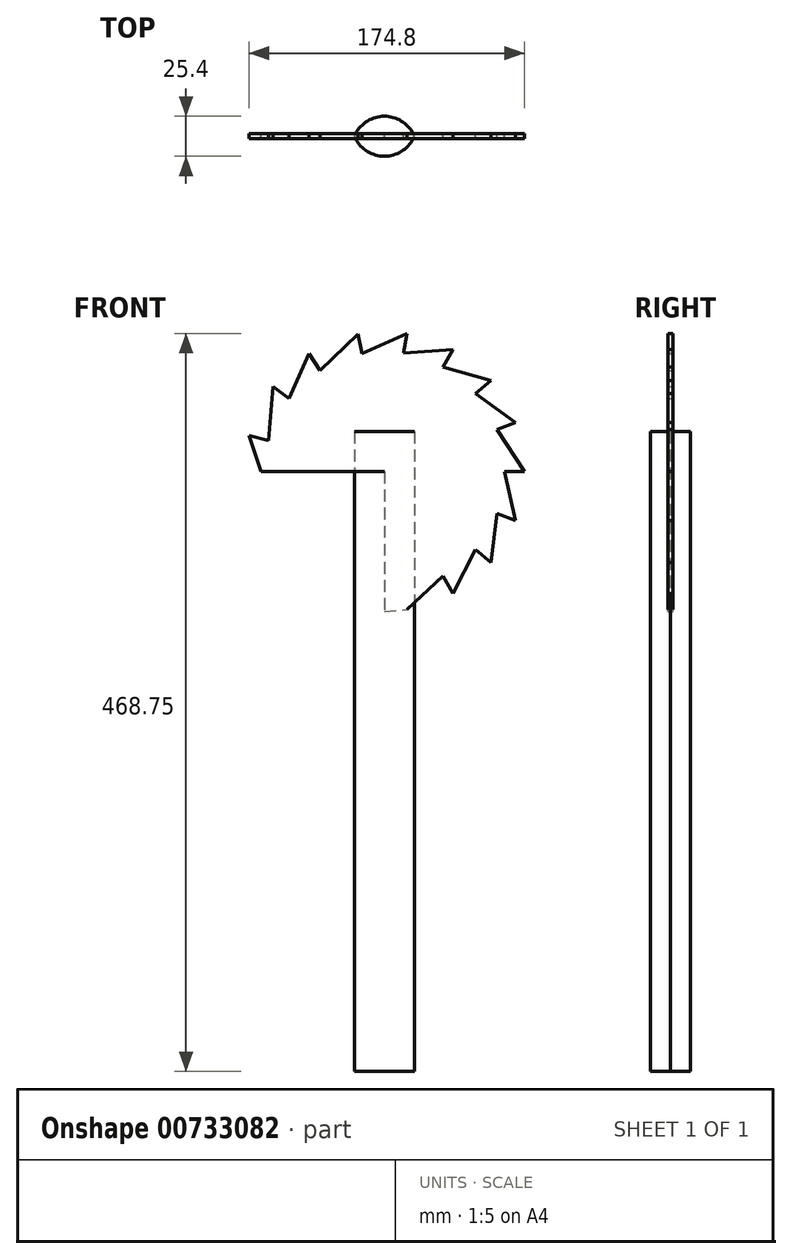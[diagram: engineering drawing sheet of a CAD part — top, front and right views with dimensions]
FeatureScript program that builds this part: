
annotation { "Feature Type Name" : "Feature", "Feature Type Description" : "" }
export const myFeature = defineFeature(function(context is Context, id is Id, definition is map)
    precondition{}
    {
        {
            var Q0;
            Q0=qCreatedBy(makeId("Top.planeOp"),FACE);
            var sketch = newSketch(context, id + "F0", { "sketchPlane" : qUnion([Q0])});
            skArc(sketch, "E0", {"start": v(19.05, 0) * mm, "mid": v(0, 12.7) * mm, "end": v(-19.05, 0) * mm});
            skArc(sketch, "E1", {"start": v(-19.05, 0) * mm, "mid": v(0, -12.7) * mm, "end": v(19.05, 0) * mm});
            skSolve(sketch);
        }
        {
            var Q0;
            Q0=makeQuery(id+"F0.imprint","IMPRINT",FACE,{"disambiguationData":[TD([[makeQuery(id+"F0.imprint","IMPRINT",EDGE,{"derivedFrom":sQuery(id+"F0.wireOp",EDGE,"E0")}),1.0]])]});
            extrude(context, id + "F1", {"entities" : qUnion([Q0]), "depth" : 406.4 * mm, "offsetDistance" : 25.4 * mm});
        }
        {
            var Q0;
            Q0=qCreatedBy(makeId("Front.planeOp"),FACE);
            var sketch = newSketch(context, id + "F2", { "sketchPlane" : qUnion([Q0])});
            skArc(sketch, "E2", {"start": v(0, 292.1) * mm, "mid": v(59.92, 446.67) * mm, "end": v(-88.53, 372.88) * mm, "construction": true});
            skLineSegment(sketch, "E3", {"start": v(0, 381) * mm, "end": v(43.57, 303.51) * mm, "construction": true});
            skLineSegment(sketch, "E4", {"start": v(0, 381) * mm, "end": v(67.56, 323.21) * mm, "construction": true});
            skLineSegment(sketch, "E5", {"start": v(0, 381) * mm, "end": v(83.3, 349.96) * mm, "construction": true});
            skLineSegment(sketch, "E6", {"start": v(0, 381) * mm, "end": v(88.9, 381) * mm, "construction": true});
            skLineSegment(sketch, "E7", {"start": v(0, 381) * mm, "end": v(83.3, 412.04) * mm, "construction": true});
            skLineSegment(sketch, "E8", {"start": v(0, 381) * mm, "end": v(67.56, 438.79) * mm, "construction": true});
            skLineSegment(sketch, "E9", {"start": v(0, 381) * mm, "end": v(43.57, 458.49) * mm, "construction": true});
            skLineSegment(sketch, "E10", {"start": v(0, 381) * mm, "end": v(14.28, 468.75) * mm, "construction": true});
            skLineSegment(sketch, "E11", {"start": v(-16.76, 468.3) * mm, "end": v(0, 381) * mm, "construction": true});
            skLineSegment(sketch, "E12", {"start": v(-47.8, 455.96) * mm, "end": v(0, 381) * mm, "construction": true});
            skLineSegment(sketch, "E13", {"start": v(-70.65, 434.96) * mm, "end": v(0, 381) * mm, "construction": true});
            skLineSegment(sketch, "E14", {"start": v(-85.9, 403.92) * mm, "end": v(0, 381) * mm, "construction": true});
            skLineSegment(sketch, "E15", {"start": v(14.28, 293.25) * mm, "end": v(0, 381) * mm, "construction": true});
            skLineSegment(sketch, "E16", {"start": v(0, 381) * mm, "end": v(-88.9, 381) * mm});
            skLineSegment(sketch, "E17", {"start": v(0, 381) * mm, "end": v(0, 292.1) * mm});
            skPoint(sketch, "E18.start.orphan", {"position": v(-79.81, 341.84) * mm});
            skPoint(sketch, "E19.start.orphan", {"position": v(-54.55, 310.8) * mm});
            skPoint(sketch, "E20.start.orphan", {"position": v(-27.09, 296.33) * mm});
            skLineSegment(sketch, "E21", {"start": v(14.28, 293.25) * mm, "end": v(37.35, 314.58) * mm});
            skLineSegment(sketch, "E22", {"start": v(37.35, 314.58) * mm, "end": v(43.57, 303.51) * mm});
            skLineSegment(sketch, "E23", {"start": v(57.9, 331.47) * mm, "end": v(43.57, 303.51) * mm});
            skLineSegment(sketch, "E24", {"start": v(67.56, 323.21) * mm, "end": v(57.9, 331.47) * mm});
            skLineSegment(sketch, "E25", {"start": v(83.3, 349.96) * mm, "end": v(71.4, 354.4) * mm});
            skLineSegment(sketch, "E26", {"start": v(71.4, 354.4) * mm, "end": v(67.56, 323.21) * mm});
            skLineSegment(sketch, "E27", {"start": v(88.9, 381) * mm, "end": v(76.2, 381) * mm});
            skLineSegment(sketch, "E28", {"start": v(76.2, 381) * mm, "end": v(83.3, 349.96) * mm});
            skLineSegment(sketch, "E29", {"start": v(83.3, 412.04) * mm, "end": v(71.4, 407.6) * mm});
            skLineSegment(sketch, "E30", {"start": v(71.4, 407.6) * mm, "end": v(88.9, 381) * mm});
            skLineSegment(sketch, "E31", {"start": v(67.56, 438.79) * mm, "end": v(57.9, 430.53) * mm});
            skLineSegment(sketch, "E32", {"start": v(57.9, 430.53) * mm, "end": v(83.3, 412.04) * mm});
            skLineSegment(sketch, "E33", {"start": v(43.57, 458.49) * mm, "end": v(37.35, 447.42) * mm});
            skLineSegment(sketch, "E34", {"start": v(37.35, 447.42) * mm, "end": v(67.56, 438.79) * mm});
            skLineSegment(sketch, "E35", {"start": v(14.28, 468.75) * mm, "end": v(12.24, 456.21) * mm});
            skLineSegment(sketch, "E36", {"start": v(12.24, 456.21) * mm, "end": v(43.57, 458.49) * mm});
            skLineSegment(sketch, "E37", {"start": v(-16.76, 468.3) * mm, "end": v(-14.37, 455.83) * mm});
            skLineSegment(sketch, "E38", {"start": v(-14.37, 455.83) * mm, "end": v(14.28, 468.75) * mm});
            skLineSegment(sketch, "E39", {"start": v(-47.8, 455.96) * mm, "end": v(-40.97, 445.25) * mm});
            skLineSegment(sketch, "E40", {"start": v(-40.97, 445.25) * mm, "end": v(-16.76, 468.3) * mm});
            skLineSegment(sketch, "E41", {"start": v(-70.65, 434.96) * mm, "end": v(-60.56, 427.25) * mm});
            skLineSegment(sketch, "E42", {"start": v(-60.56, 427.25) * mm, "end": v(-47.8, 455.96) * mm});
            skLineSegment(sketch, "E43", {"start": v(-85.9, 403.92) * mm, "end": v(-73.62, 400.64) * mm});
            skLineSegment(sketch, "E44", {"start": v(-73.62, 400.64) * mm, "end": v(-70.65, 434.96) * mm});
            skLineSegment(sketch, "E45", {"start": v(-75.9, 374.13) * mm, "end": v(-85.9, 403.92) * mm});
            skLineSegment(sketch, "E46", {"start": v(-88.53, 372.88) * mm, "end": v(-75.9, 374.13) * mm, "construction": true});
            skLineSegment(sketch, "E47", {"start": v(0, 292.1) * mm, "end": v(14.28, 293.25) * mm});
            skSolve(sketch);
        }
        {
            var Q0;
            {var subQ0=sQuery(id+"F2.wireOp",EDGE,"E17");Q0=makeQuery(id+"F2.imprint","IMPRINT",FACE,{"disambiguationData":[TD([[makeQuery(id+"F2.imprint","IMPRINT",EDGE,{"derivedFrom":subQ0}),1.0]])]});}
            extrude(context, id + "F3", {"entities" : qUnion([Q0]), "depth" : 1.59 * mm, "offsetDistance" : 25.4 * mm, "hasSecondDirection" : true, "secondDirectionOppositeDirection" : true, "secondDirectionDepth" : 1.59 * mm});
        }
    });
